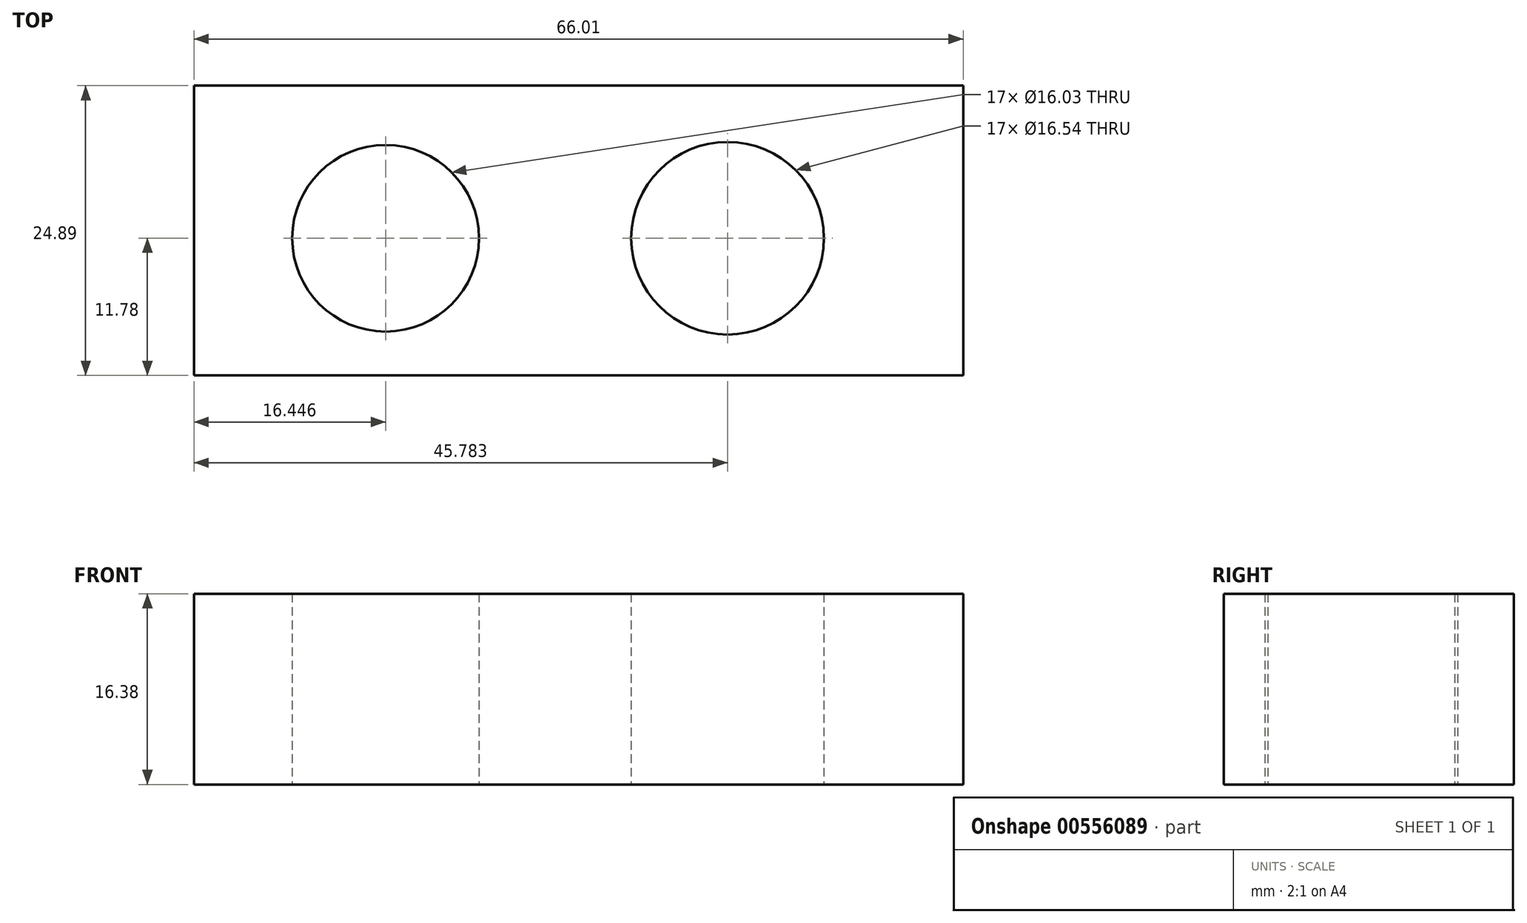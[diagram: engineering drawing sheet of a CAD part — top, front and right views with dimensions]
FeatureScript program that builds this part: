
annotation { "Feature Type Name" : "Feature", "Feature Type Description" : "" }
export const myFeature = defineFeature(function(context is Context, id is Id, definition is map)
    precondition{}
    {
        {
            var Q0;
            Q0=qCreatedBy(makeId("Top.planeOp"),FACE);
            var sketch = newSketch(context, id + "F0", { "sketchPlane" : qUnion([Q0])});
            skLineSegment(sketch, "E0", {"start": v(-41.56, 34.9) * mm, "end": v(24.45, 34.9) * mm});
            skLineSegment(sketch, "E1", {"start": v(-41.56, 34.9) * mm, "end": v(-41.56, 10) * mm});
            skLineSegment(sketch, "E2", {"start": v(24.45, 34.9) * mm, "end": v(24.45, 10) * mm});
            skLineSegment(sketch, "E3", {"start": v(-41.56, 10) * mm, "end": v(24.45, 10) * mm});
            skSolve(sketch);
        }
        {
            var Q0;
            Q0=makeQuery(id+"F0.imprint","IMPRINT",FACE,{"disambiguationData":[TD([[makeQuery(id+"F0.imprint","IMPRINT",EDGE,{"derivedFrom":sQuery(id+"F0.wireOp",EDGE,"E0")}),-1.0]])]});
            var sketch = newSketch(context, id + "F1", { "sketchPlane" : qUnion([Q0])});
            skCircle(sketch, "E4", {"center": v(-25.11, 21.78) * mm, "radius": 8.01 * mm});
            skLineSegment(sketch, "E5", {"start": v(-25.11, 21.78) * mm, "end": v(4.22, 21.78) * mm});
            skCircle(sketch, "E6", {"center": v(4.22, 21.78) * mm, "radius": 8.27 * mm});
            skSolve(sketch);
        }
        {
            var Q0;
            Q0=makeQuery(id+"F1.imprint","IMPRINT",FACE,{"disambiguationData":[TD([[makeQuery(id+"F1.imprint","IMPRINT",EDGE,{"derivedFrom":sQuery(id+"F1.wireOp",EDGE,"E4")}),-1.0]])]});
            extrude(context, id + "F2", {"entities" : qUnion([Q0]), "depth" : 16.38 * mm, "offsetDistance" : 25.4 * mm});
        }
    });
